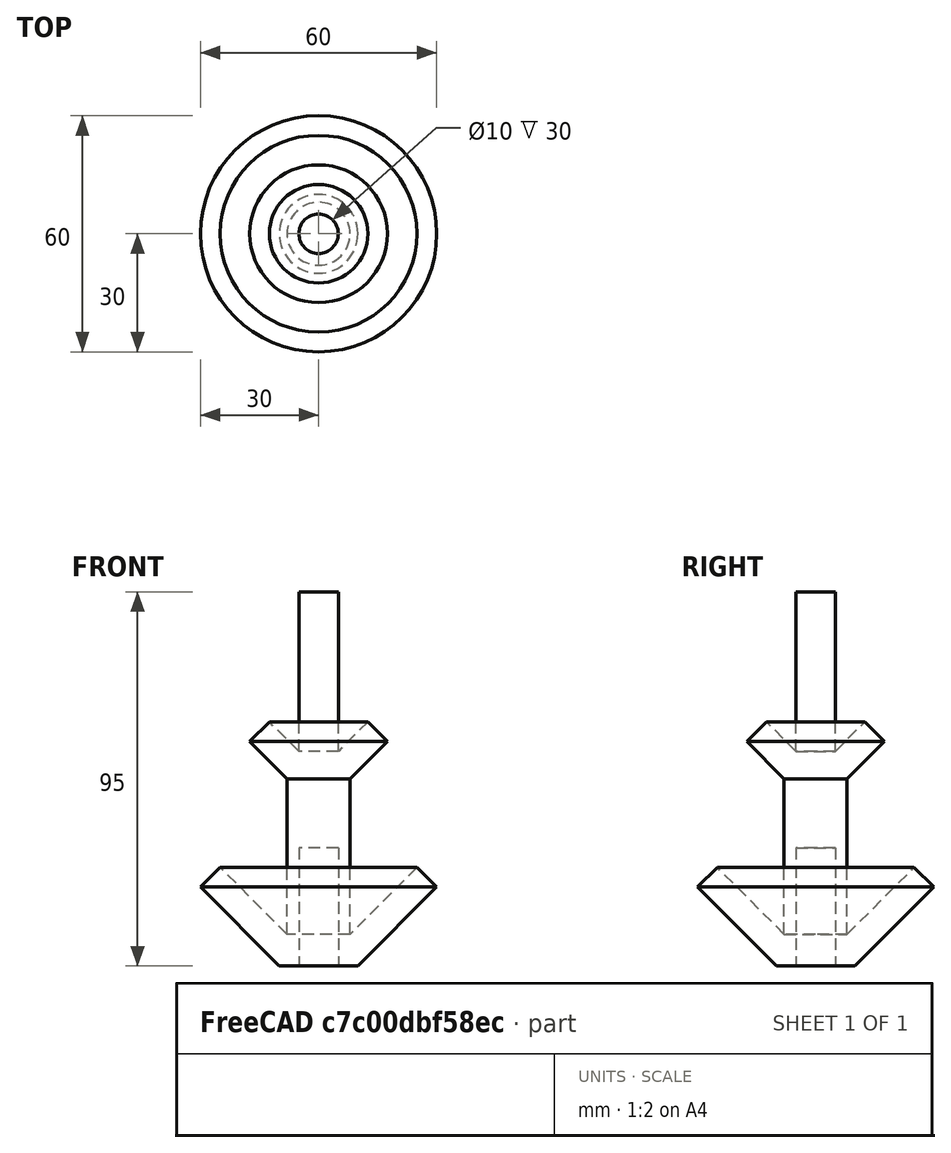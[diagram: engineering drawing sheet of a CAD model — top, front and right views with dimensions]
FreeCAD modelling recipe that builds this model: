
FCSTD DOCUMENT  (FreeCAD 0.18.4R)
Label: part17
License: All rights reserved
LicenseURL: http://en.wikipedia.org/wiki/All_rights_reserved
objects: Sketcher::SketchObject×1, PartDesign::Revolution×1, PartDesign::Body×1
note: 4 computed .brp shape members not serialized (recipe doc carries the construction recipe); baked Part::Feature solids carry a one-line shape summary decoded from their .brp

FEATURE [Sketcher::SketchObject] Sketch
  MapMode = 5
  Placement = pos=(0,0,0) rot=(1,0,0;1.5708rad)
  Support = -> [XZ_Plane]
  sketch-geometry (13):
    g0: LineSegment StartX=0 StartY=30 StartZ=0 EndX=5 EndY=30 EndZ=0
    g1: LineSegment StartX=5 StartY=30 StartZ=0 EndX=5 EndY=0 EndZ=0
    g2: LineSegment StartX=5 StartY=0 StartZ=0 EndX=10 EndY=0 EndZ=0
    g3: LineSegment StartX=10 StartY=0 StartZ=0 EndX=30 EndY=20 EndZ=0
    g4: LineSegment StartX=30 StartY=20 StartZ=0 EndX=25 EndY=25 EndZ=0
    g5: LineSegment StartX=25 StartY=25 StartZ=0 EndX=8 EndY=8 EndZ=0
    g6: LineSegment StartX=8 StartY=8 StartZ=0 EndX=8 EndY=47.5 EndZ=0
    g7: LineSegment StartX=8 StartY=47.5 StartZ=0 EndX=17.5 EndY=57 EndZ=0
    g8: LineSegment StartX=17.5 StartY=57 StartZ=0 EndX=12.5 EndY=62 EndZ=0
    g9: LineSegment StartX=12.5 StartY=62 StartZ=0 EndX=5 EndY=54.5 EndZ=0
    g10: LineSegment StartX=5 StartY=54.5 StartZ=0 EndX=5 EndY=95 EndZ=0
    g11: LineSegment StartX=5 StartY=95 StartZ=0 EndX=0 EndY=95 EndZ=0
    g12: LineSegment StartX=0 StartY=95 StartZ=0 EndX=0 EndY=30 EndZ=0
  constraints (39):
    c: Horizontal(g0)
    c: Coincident(g0,g1)
    c: Vertical(g1)
    c: Coincident(g1,g2)
    c: Horizontal(g2)
    c: Coincident(g2,g3)
    c: Coincident(g3,g4)
    c: Coincident(g4,g5)
    c: Coincident(g5,g6)
    c: Vertical(g6)
    c: Coincident(g6,g7)
    c: Coincident(g7,g8)
    c: Coincident(g8,g9)
    c: Coincident(g9,g10)
    c: Vertical(g10)
    c: Coincident(g10,g11)
    c: Horizontal(g11)
    c: Coincident(g11,g12)
    c: Coincident(g12,g0)
    c: Vertical(g12)
    c: Perpendicular(g3,g4)
    c: Perpendicular(g7,g8)
    c: PointOnObject(g0,g-2)
    c: PointOnObject(g1,g-1)
    c: DistanceX(g0,g0) = 5
    c: Angle(g3,g2) = 2.35619
    c: DistanceX(g-1,g3) = 30
    c: DistanceY(g3,g4) = 5
    c: DistanceY(g-1,g11) = 95
    c: DistanceX(g11,g11) = 5
    c: Angle(g6,g7) = 2.35619
    c: DistanceY(g7,g8) = 5
    c: DistanceX(g-1,g7) = 17.5
    c: DistanceX(g-1,g5) = 8
    c: Perpendicular(g4,g5)
    c: Perpendicular(g9,g8)
    c: DistanceY(g-1,g0) = 30
    c: DistanceX(g-1,g2) = 10
    c: DistanceY(g-1,g6) = 47.5
FEATURE [PartDesign::Revolution] Revolution
  Angle = 360
  Axis = (-3e-16,3e-16,1)
  Base = (0,0,0)
  Placement = pos=(0,0,0) rot=(1,0,0;1.5708rad)
  Profile = -> Sketch
  ReferenceAxis = -> Z_Axis
  Reversed = true
FEATURE [PartDesign::Body] Body
  Group = -> [Sketch,Revolution]
  Origin = -> Origin
  Tip = -> Revolution
